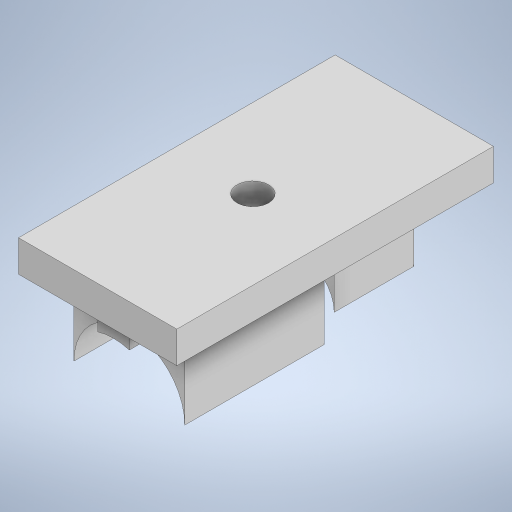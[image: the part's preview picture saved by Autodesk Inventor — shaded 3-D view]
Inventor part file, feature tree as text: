
AUTODESK INVENTOR PART (.ipt)
format: ipt  version: 2023 (Build 270158000, 158)  size: 311,296 bytes
history: native  units: in
note: dims shown in document units (in); Inventor stores cm internally (conversion verified against a paired STEP export)
features: extrude x6, plane x6, sketch x4, projected_geometry x3
ambient origin geometry x8: Origin, YZ Plane, XZ Plane, XY Plane, X Axis, Y Axis, Z Axis, Center Point
bodies: Solid1 (feature_tree)
feature tree (19):
  sketch  "Sketch1"  dims[d0=1.9685in d1=3.937in d2=1.7323in d3=90.0deg d4=1.378in d5=0.3937in d6=0.9882in d7=90.0deg d8=0.8071in d9=0.1969in d10=90.0deg d11=0.0in d12=0.3937in d13=0.0in]
  extrude  "Extrusion1"  Depth=0.3937in TaperAngle=0.0deg
  plane  "Work Plane1"
  plane  "Work Plane2"
  plane  "Work Plane3"
  plane  "Work Plane4"
  sketch  "Sketch2"  dims[d14=1.9685in d15=1.9685in]
  sketch  "Sketch3"  dims[d16=0.8071in d17=1.9685in]
  sketch  "Sketch4"  dims[d18=1.9685in d19=1.378in d20=1.9685in d21=1.9685in d22=0.3937in d23=0.3937in d24=0.1969in d25=0.3937in d26=0.3937in d27=0.0in d28=0.3937in d29=0.0in d30=0.3937in d31=0.0in d32=0.3937in d33=0.0in d34=0.3937in d35=0.0in]
  plane  "Work Plane5"
  extrude  "Extrusion2"  Depth=1.9685in
  extrude  "Extrusion3"  Depth=1.9685in
  plane  "Work Plane6"
  extrude  "Extrusion4"  Depth=1.378in
  extrude  "Extrusion5"  Depth=1.9685in
  extrude  "Extrusion6"  Depth=1.9685in
  projected_geometry  "Projected Loop1"
  projected_geometry  "Projected Loop2"
  projected_geometry  "Projected Loop3"
